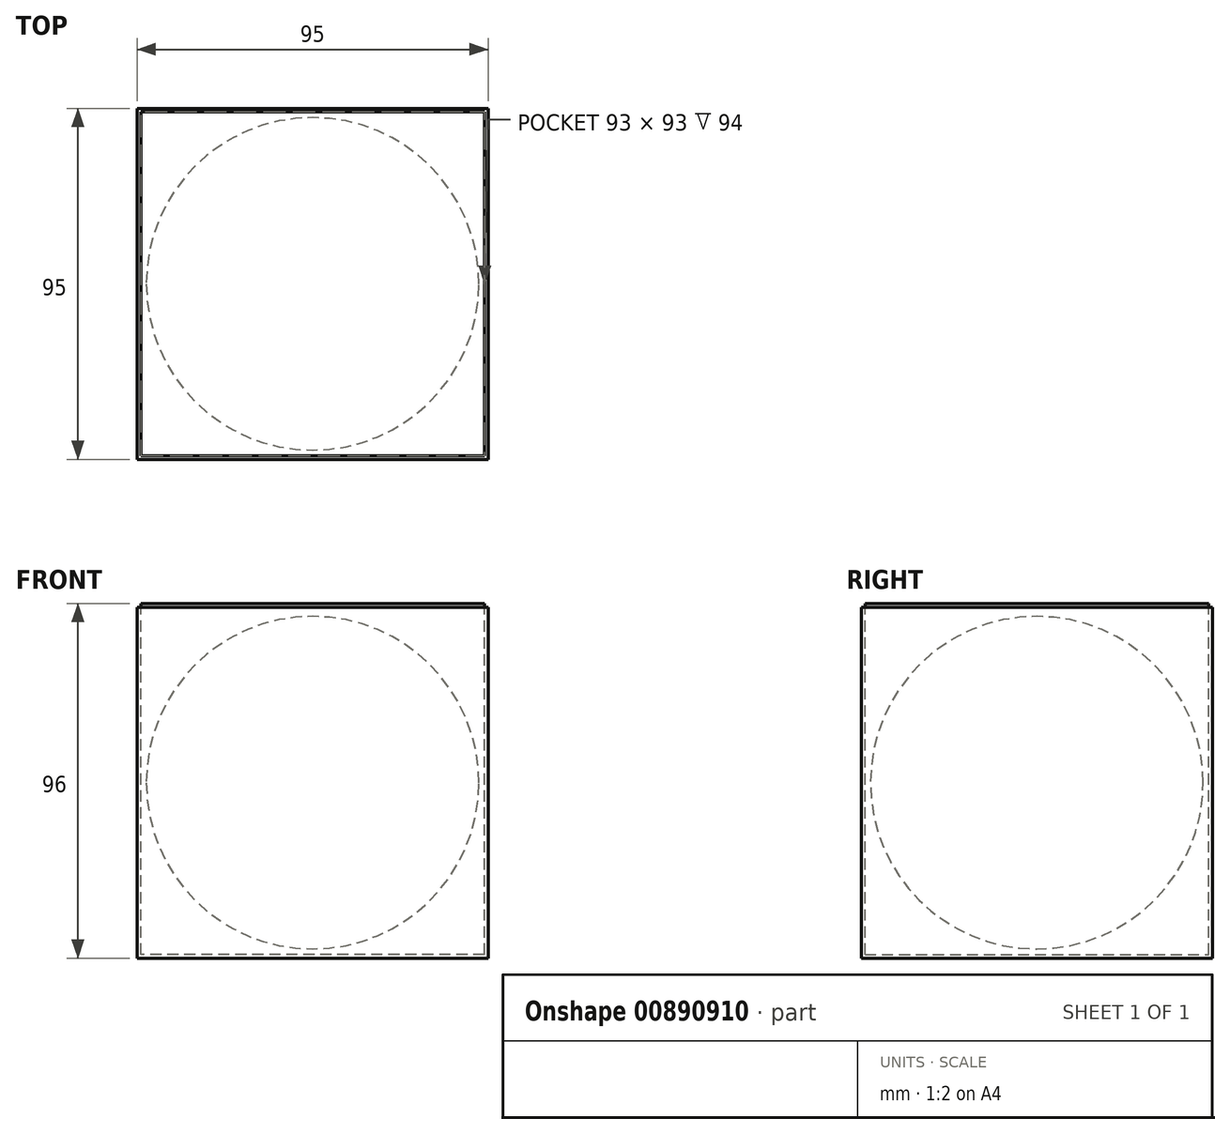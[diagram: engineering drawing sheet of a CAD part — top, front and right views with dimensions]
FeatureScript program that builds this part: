
annotation { "Feature Type Name" : "Feature", "Feature Type Description" : "" }
export const myFeature = defineFeature(function(context is Context, id is Id, definition is map)
    precondition{}
    {
        {
            var Q0;
            Q0=qCreatedBy(makeId("Front.planeOp"),FACE);
            var sketch = newSketch(context, id + "F0", { "sketchPlane" : qUnion([Q0])});
            skArc(sketch, "E0", {"start": v(45, 0) * mm, "mid": v(0, 45) * mm, "end": v(-45, 0) * mm});
            skLineSegment(sketch, "E1", {"start": v(-45, 0) * mm, "end": v(45, 0) * mm});
            skSolve(sketch);
        }
        {
            var Q0;
            Q0=makeQuery(id+"F0.imprint","IMPRINT",FACE,{"disambiguationData":[TD([[makeQuery(id+"F0.imprint","IMPRINT",EDGE,{"derivedFrom":sQuery(id+"F0.wireOp",EDGE,"E0")}),1.0]])]});
            var Q1;
            Q1=sQuery(id+"F0.wireOp",EDGE,"E1");
            revolve(context, id + "F1", {"surfaceOperationType" : NewSurfaceOperationType.NEW, "entities" : qUnion([Q0]), "axis" : qUnion([Q1]), "revolveType" : RevolveType.FULL});
        }
        {
            var Q0;
            Q0=qCreatedBy(makeId("Front.planeOp"),FACE);
            var sketch = newSketch(context, id + "F2", { "sketchPlane" : qUnion([Q0])});
            skLineSegment(sketch, "E2.bottom", {"start": v(47.5, -47.5) * mm, "end": v(-47.5, -47.5) * mm});
            skLineSegment(sketch, "E2.top", {"start": v(47.5, 47.5) * mm, "end": v(-47.5, 47.5) * mm});
            skLineSegment(sketch, "E2.left", {"start": v(47.5, -47.5) * mm, "end": v(47.5, 47.5) * mm});
            skLineSegment(sketch, "E2.right", {"start": v(-47.5, -47.5) * mm, "end": v(-47.5, 47.5) * mm});
            skPoint(sketch, "E2.middle", {"position": v(0, 0) * mm});
            skSolve(sketch);
        }
        {
            var Q0;
            Q0=makeQuery(id+"F2.imprint","IMPRINT",FACE,{"disambiguationData":[TD([[makeQuery(id+"F2.imprint","IMPRINT",EDGE,{"derivedFrom":sQuery(id+"F2.wireOp",EDGE,"E2.bottom")}),-1.0]])]});
            extrude(context, id + "F3", {"entities" : qUnion([Q0]), "endBound" : BoundingType.SYMMETRIC, "depth" : 95 * mm, "offsetDistance" : 25 * mm});
        }
        {
            var Q0;
            Q0=makeQuery(id+"F3.opExtrude","SWEPT_FACE",FACE,{"disambiguationData":[OSD([sQuery(id+"F2.wireOp",EDGE,"E2.top")])]});
            shell(context, id + "F4", {"entities" : qUnion([Q0]), "thickness" : 1 * mm});
        }
        {
            var Q0;
            Q0=makeQuery(id+"F3.opExtrude","SWEPT_FACE",FACE,{"disambiguationData":[OSD([sQuery(id+"F2.wireOp",EDGE,"E2.top")])]});
            var sketch = newSketch(context, id + "F5", { "sketchPlane" : qUnion([Q0])});
            skLineSegment(sketch, "E3.bottom", {"start": v(-46.5, 46.5) * mm, "end": v(46.5, 46.5) * mm});
            skLineSegment(sketch, "E3.top", {"start": v(-46.5, -46.5) * mm, "end": v(46.5, -46.5) * mm});
            skLineSegment(sketch, "E3.left", {"start": v(-46.5, 46.5) * mm, "end": v(-46.5, -46.5) * mm});
            skLineSegment(sketch, "E3.right", {"start": v(46.5, 46.5) * mm, "end": v(46.5, -46.5) * mm});
            skPoint(sketch, "E3.middle", {"position": v(0, 0) * mm});
            skSolve(sketch);
        }
        {
            var Q0;
            Q0=makeQuery(id+"F5.imprint","IMPRINT",FACE,{"disambiguationData":[TD([[makeQuery(id+"F5.imprint","IMPRINT",EDGE,{"derivedFrom":sQuery(id+"F5.wireOp",EDGE,"E3.bottom")}),1.0]])]});
            extrude(context, id + "F6", {"entities" : qUnion([Q0]), "depth" : 1 * mm, "offsetDistance" : 25 * mm});
        }
    });
